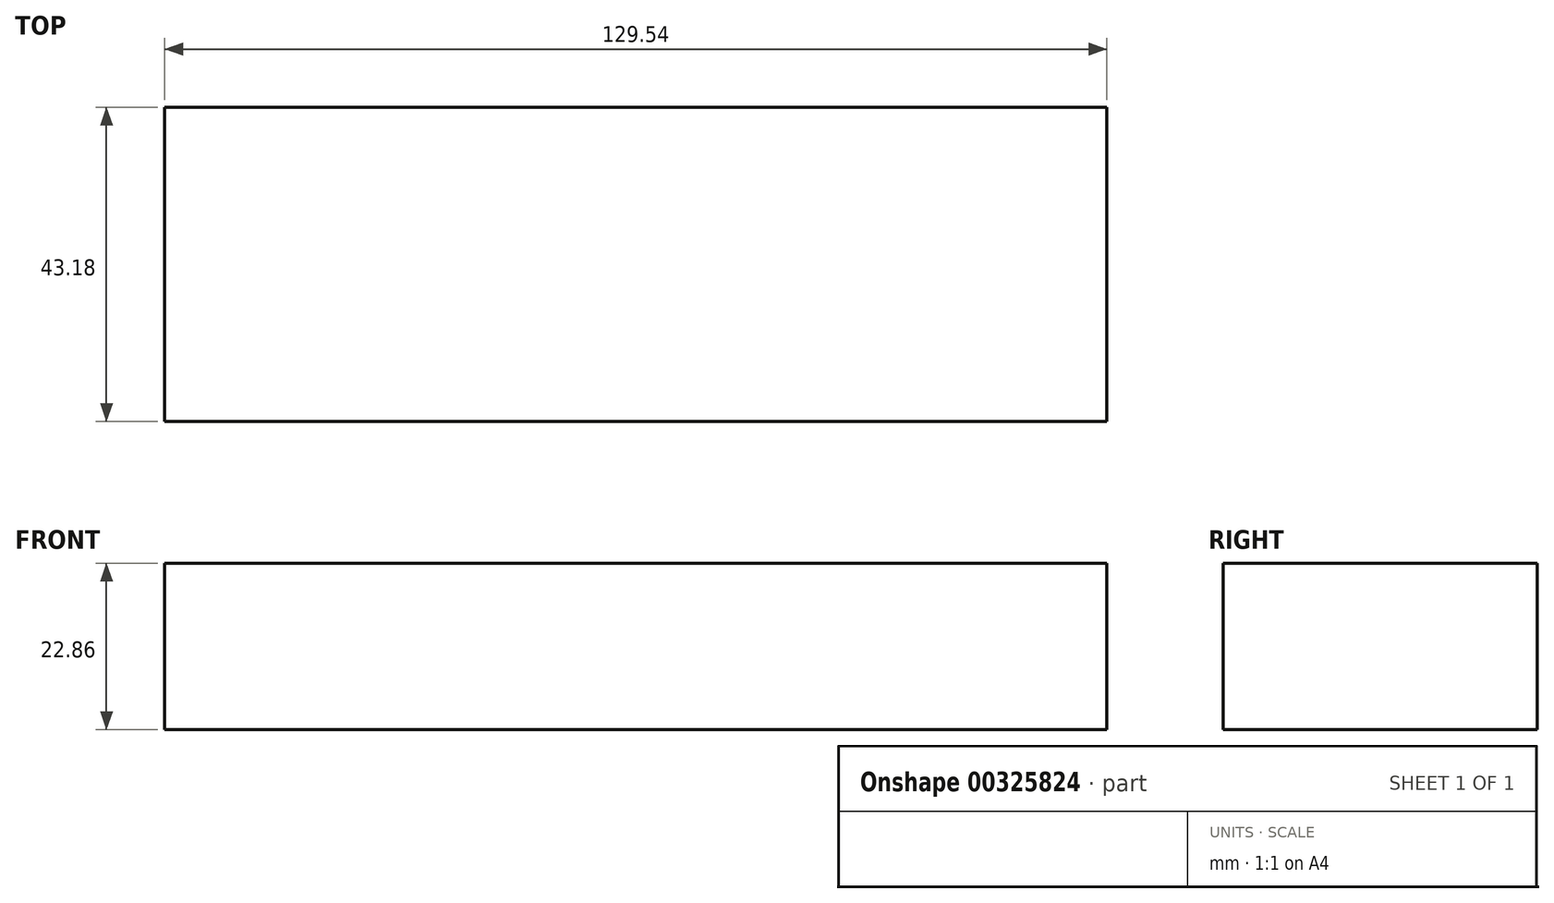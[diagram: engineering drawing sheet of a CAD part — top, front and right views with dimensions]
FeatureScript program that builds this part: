
annotation { "Feature Type Name" : "Feature", "Feature Type Description" : "" }
export const myFeature = defineFeature(function(context is Context, id is Id, definition is map)
    precondition{}
    {
        {
            var Q0;
            Q0=qCreatedBy(makeId("Top.planeOp"),FACE);
            var sketch = newSketch(context, id + "F0", { "sketchPlane" : qUnion([Q0])});
            skLineSegment(sketch, "E0.bottom", {"start": v(-64.77, 21.6) * mm, "end": v(64.77, 21.59) * mm});
            skLineSegment(sketch, "E0.top", {"start": v(-64.77, -21.59) * mm, "end": v(64.77, -21.6) * mm});
            skLineSegment(sketch, "E0.left", {"start": v(-64.77, 21.6) * mm, "end": v(-64.77, -21.6) * mm});
            skLineSegment(sketch, "E0.right", {"start": v(64.77, 21.6) * mm, "end": v(64.77, -21.6) * mm});
            skLineSegment(sketch, "E1", {"start": v(0, 0) * mm, "end": v(0, 47.62) * mm, "construction": true});
            skLineSegment(sketch, "E2", {"start": v(0, 0) * mm, "end": v(95.8, 0) * mm, "construction": true});
            skSolve(sketch);
        }
        {
            var Q0;
            Q0=makeQuery(id+"F0.imprint","IMPRINT",FACE,{"disambiguationData":[TD([[makeQuery(id+"F0.imprint","IMPRINT",EDGE,{"derivedFrom":sQuery(id+"F0.wireOp",EDGE,"E0.bottom")}),-1.0]])]});
            extrude(context, id + "F1", {"entities" : qUnion([Q0]), "depth" : 22.86 * mm});
        }
    });
